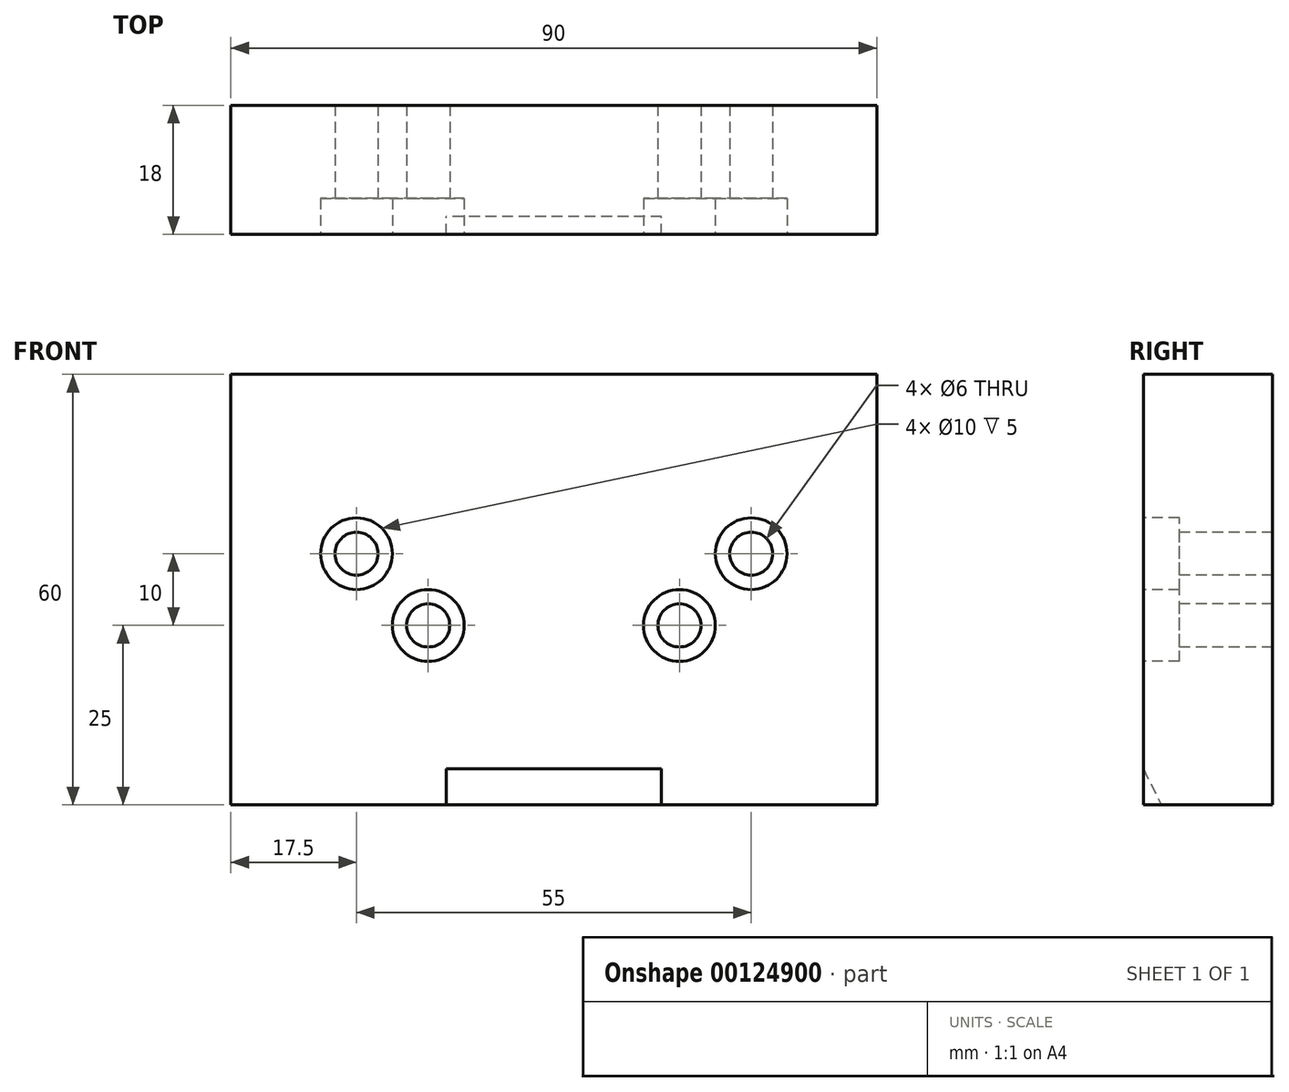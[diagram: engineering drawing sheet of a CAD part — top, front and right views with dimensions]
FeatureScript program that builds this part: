
annotation { "Feature Type Name" : "Feature", "Feature Type Description" : "" }
export const myFeature = defineFeature(function(context is Context, id is Id, definition is map)
    precondition{}
    {
        {
            var Q0;
            Q0=qCreatedBy(makeId("Front.planeOp"),FACE);
            var sketch = newSketch(context, id + "F0", { "sketchPlane" : qUnion([Q0])});
            skLineSegment(sketch, "E0.bottom", {"start": v(-45, 0) * mm, "end": v(45, 0) * mm});
            skLineSegment(sketch, "E0.top", {"start": v(-45, 60) * mm, "end": v(45, 60) * mm});
            skLineSegment(sketch, "E0.left", {"start": v(-45, 0) * mm, "end": v(-45, 60) * mm});
            skLineSegment(sketch, "E0.right", {"start": v(45, 0) * mm, "end": v(45, 60) * mm});
            skLineSegment(sketch, "E1", {"start": v(0, 60) * mm, "end": v(0, 0) * mm, "construction": true});
            skSolve(sketch);
        }
        {
            var Q0;
            Q0 = qSketchRegion(id + "F0", true);
            extrude(context, id + "F1", {"entities" : qUnion([Q0]), "depth" : 18 * mm});
        }
        {
            var Q0;
            Q0=makeQuery(id+"F1.opExtrude","CAP_FACE",FACE,{"disambiguationData":[OSD([sQuery(id+"F0.wireOp",EDGE,"E0.bottom"),sQuery(id+"F0.wireOp",EDGE,"E0.top"),sQuery(id+"F0.wireOp",EDGE,"E0.left"),sQuery(id+"F0.wireOp",EDGE,"E0.right")])],"isStart":false});
            var sketch = newSketch(context, id + "F2", { "sketchPlane" : qUnion([Q0])});
            skPoint(sketch, "E2", {"position": v(-27.5, 35) * mm});
            skPoint(sketch, "E3", {"position": v(-17.5, 25) * mm});
            skLineSegment(sketch, "E4", {"start": v(0, 0) * mm, "end": v(0, 60) * mm, "construction": true});
            skPoint(sketch, "E5", {"position": v(27.5, 35) * mm});
            skPoint(sketch, "E6", {"position": v(17.5, 25) * mm});
            skSolve(sketch);
        }
        {
            var Q0;
            Q0=sQuery(id+"F2.wireOp",VERTEX,"E2");
            var Q1;
            Q1=sQuery(id+"F2.wireOp",VERTEX,"E3");
            var Q2;
            Q2=sQuery(id+"F2.wireOp",VERTEX,"E6");
            var Q3;
            Q3=sQuery(id+"F2.wireOp",VERTEX,"E5");
            var Q4;
            Q4=makeQuery(id+"F1.opExtrude","SWEPT_BODY",BODY,{"disambiguationData":[OSD([sQuery(id+"F0.wireOp",EDGE,"E0.bottom"),sQuery(id+"F0.wireOp",EDGE,"E0.top"),sQuery(id+"F0.wireOp",EDGE,"E0.left"),sQuery(id+"F0.wireOp",EDGE,"E0.right")])]});
            hole(context, id + "F3", {"style" : HoleStyle.C_BORE, "endStyle" : HoleEndStyle.THROUGH, "holeDiameter" : 6 * mm, "cBoreDiameter" : 10 * mm, "cBoreDepth" : 5 * mm, "locations" : qUnion([Q0, Q1, Q2, Q3]), "scope" : qUnion([Q4]), "isTappedThrough" : true});
        }
        {
            var Q0;
            Q0=makeQuery(id+"F1.opExtrude","SWEPT_FACE",FACE,{"disambiguationData":[OSD([sQuery(id+"F0.wireOp",EDGE,"E0.right")])]});
            cPlane(context, id + "F4", {"entities" : qUnion([Q0]), "cplaneType" : CPlaneType.OFFSET, "offset" : 30 * mm, "oppositeDirection" : true, "width" : 150 * mm, "height" : 150 * mm});
        }
        {
            var Q0;
            Q0=makeQuery(id+"F1.opExtrude","SWEPT_FACE",FACE,{"disambiguationData":[OSD([sQuery(id+"F0.wireOp",EDGE,"E0.left")])]});
            cPlane(context, id + "F5", {"entities" : qUnion([Q0]), "cplaneType" : CPlaneType.OFFSET, "offset" : 30 * mm, "oppositeDirection" : true, "width" : 150 * mm, "height" : 150 * mm});
        }
        {
            var Q0;
            Q0=qCreatedBy(id+"F5.planeOp",FACE);
            var sketch = newSketch(context, id + "F6", { "sketchPlane" : qUnion([Q0])});
            skLineSegment(sketch, "E7.0", {"start": v(18, 0) * mm, "end": v(0, 0) * mm});
            skLineSegment(sketch, "E8", {"start": v(2.5, 0) * mm, "end": v(0, 0) * mm});
            skLineSegment(sketch, "E9.0", {"start": v(18, 0) * mm, "end": v(18, 60) * mm});
            skLineSegment(sketch, "E10", {"start": v(18, 5) * mm, "end": v(15.5, 0) * mm});
            skLineSegment(sketch, "E11", {"start": v(18, 5) * mm, "end": v(18, 0) * mm});
            skLineSegment(sketch, "E12", {"start": v(15.5, 0) * mm, "end": v(18, 0) * mm});
            skSolve(sketch);
        }
        {
            var Q0;
            Q0 = qSketchRegion(id + "F6", true);
            var Q1;
            Q1=qCreatedBy(id+"F4.planeOp",FACE);
            var Q2;
            Q2=qCreatedBy(id+"F5.planeOp",FACE);
            extrude(context, id + "F7", {"entities" : qUnion([Q0]), "operationType" : NewBodyOperationType.REMOVE, "endBound" : BoundingType.UP_TO_SURFACE, "oppositeDirection" : true, "endBoundEntityFace" : qUnion([Q1]), "depth" : 25 * mm});
        }
    });
